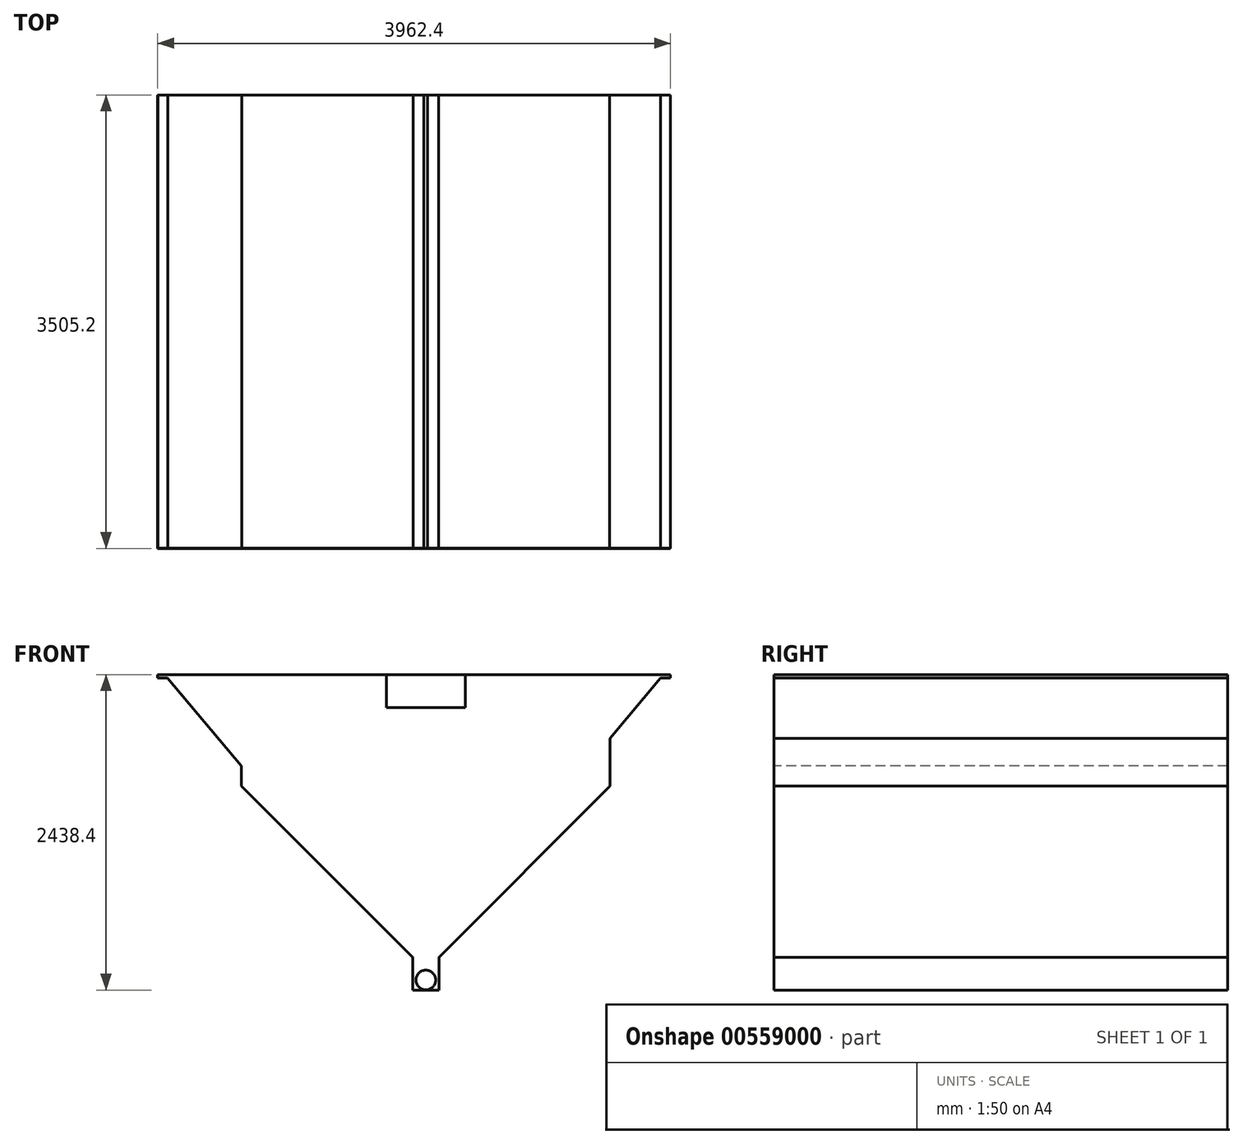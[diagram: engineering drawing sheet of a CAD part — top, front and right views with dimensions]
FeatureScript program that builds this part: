
annotation { "Feature Type Name" : "Feature", "Feature Type Description" : "" }
export const myFeature = defineFeature(function(context is Context, id is Id, definition is map)
    precondition{}
    {
        {
            var Q0;
            Q0=qCreatedBy(makeId("Front.planeOp"),FACE);
            var sketch = newSketch(context, id + "F0", { "sketchPlane" : qUnion([Q0])});
            skLineSegment(sketch, "E0", {"start": v(1891.4, 2159) * mm, "end": v(1891.4, 2184.4) * mm});
            skLineSegment(sketch, "E1", {"start": v(1891.4, 2159) * mm, "end": v(1815.2, 2159) * mm});
            skLineSegment(sketch, "E2", {"start": v(-1994.8, 2184.4) * mm, "end": v(-2071, 2184.4) * mm});
            skLineSegment(sketch, "E3", {"start": v(-2071, 2184.4) * mm, "end": v(-2071, 2159) * mm});
            skLineSegment(sketch, "E4", {"start": v(-2071, 2159) * mm, "end": v(-1994.8, 2159) * mm});
            skLineSegment(sketch, "E5", {"start": v(-1423.36, 1477.99) * mm, "end": v(-1994.8, 2159) * mm});
            skLineSegment(sketch, "E6", {"start": v(1891.4, 2184.4) * mm, "end": v(1815.2, 2184.4) * mm});
            skLineSegment(sketch, "E7", {"start": v(1815.2, 2184.4) * mm, "end": v(-1994.8, 2184.4) * mm});
            skLineSegment(sketch, "E8", {"start": v(1815.2, 2159) * mm, "end": v(1423.36, 1692.02) * mm});
            skLineSegment(sketch, "E9", {"start": v(-1423.36, 1477.99) * mm, "end": v(-1423.36, 1321.76) * mm});
            skLineSegment(sketch, "E10", {"start": v(1423.36, 1692.02) * mm, "end": v(1423.36, 1321.76) * mm});
            skLineSegment(sketch, "E11", {"start": v(0, 3707.85) * mm, "end": v(0, -913.4) * mm, "construction": true});
            skLineSegment(sketch, "E12", {"start": v(-1423.36, 1321.76) * mm, "end": v(-101.6, 0) * mm});
            skLineSegment(sketch, "E13", {"start": v(-101.6, 0) * mm, "end": v(-101.6, -254) * mm});
            skLineSegment(sketch, "E14", {"start": v(101.6, -254) * mm, "end": v(101.6, 0) * mm});
            skLineSegment(sketch, "E15", {"start": v(101.6, 0) * mm, "end": v(1423.36, 1321.76) * mm});
            skLineSegment(sketch, "E16", {"start": v(-1994.8, 2184.4) * mm, "end": v(-1994.8, 2159) * mm});
            skLineSegment(sketch, "E17", {"start": v(1815.2, 2184.4) * mm, "end": v(1815.2, 2159) * mm});
            skLineSegment(sketch, "E18", {"start": v(-101.6, -254) * mm, "end": v(101.6, -254) * mm});
            skSolve(sketch);
        }
        {
            var Q0;
            Q0 = qSketchRegion(id + "F0", true);
            extrude(context, id + "F1", {"entities" : qUnion([Q0]), "oppositeDirection" : true, "depth" : 3505.2 * mm, "offsetDistance" : 25.4 * mm});
        }
        {
            var Q0;
            Q0=makeQuery(id+"F1.opExtrude","SWEPT_FACE",FACE,{"disambiguationData":[OSD([sQuery(id+"F0.wireOp",EDGE,"E2"),sQuery(id+"F0.wireOp",EDGE,"E6"),sQuery(id+"F0.wireOp",EDGE,"E7")])]});
            shell(context, id + "F2", {"entities" : qUnion([Q0]), "thickness" : 2.54 * mm});
        }
        {
            var Q0;
            Q0=makeQuery(id+"F1.opExtrude","CAP_FACE",FACE,{"disambiguationData":[OSD([sQuery(id+"F0.wireOp",EDGE,"E0"),sQuery(id+"F0.wireOp",EDGE,"E1"),sQuery(id+"F0.wireOp",EDGE,"E2"),sQuery(id+"F0.wireOp",EDGE,"E3"),sQuery(id+"F0.wireOp",EDGE,"E4"),sQuery(id+"F0.wireOp",EDGE,"E5"),sQuery(id+"F0.wireOp",EDGE,"E6"),sQuery(id+"F0.wireOp",EDGE,"E7"),sQuery(id+"F0.wireOp",EDGE,"E8"),sQuery(id+"F0.wireOp",EDGE,"E9"),sQuery(id+"F0.wireOp",EDGE,"E10"),sQuery(id+"F0.wireOp",EDGE,"E12"),sQuery(id+"F0.wireOp",EDGE,"E13"),sQuery(id+"F0.wireOp",EDGE,"E14"),sQuery(id+"F0.wireOp",EDGE,"E15"),sQuery(id+"F0.wireOp",EDGE,"E18")])],"isStart":true});
            var sketch = newSketch(context, id + "F3", { "sketchPlane" : qUnion([Q0])});
            skCircle(sketch, "E19", {"center": v(0, -176.53) * mm, "radius": 76.2 * mm});
            skSolve(sketch);
        }
        {
            var Q0;
            Q0=makeQuery(id+"F3.imprint","IMPRINT",FACE,{"disambiguationData":[TD([[makeQuery(id+"F3.imprint","IMPRINT",EDGE,{"derivedFrom":sQuery(id+"F3.wireOp",EDGE,"E19")}),1.0]])]});
            extrude(context, id + "F4", {"entities" : qUnion([Q0]), "operationType" : NewBodyOperationType.REMOVE, "endBound" : BoundingType.THROUGH_ALL, "oppositeDirection" : true, "depth" : 25.4 * mm, "offsetDistance" : 25.4 * mm});
        }
        {
            var Q0;
            Q0=makeQuery(id+"F1.opExtrude","CAP_FACE",FACE,{"disambiguationData":[OSD([sQuery(id+"F0.wireOp",EDGE,"E0"),sQuery(id+"F0.wireOp",EDGE,"E1"),sQuery(id+"F0.wireOp",EDGE,"E2"),sQuery(id+"F0.wireOp",EDGE,"E3"),sQuery(id+"F0.wireOp",EDGE,"E4"),sQuery(id+"F0.wireOp",EDGE,"E5"),sQuery(id+"F0.wireOp",EDGE,"E6"),sQuery(id+"F0.wireOp",EDGE,"E7"),sQuery(id+"F0.wireOp",EDGE,"E8"),sQuery(id+"F0.wireOp",EDGE,"E9"),sQuery(id+"F0.wireOp",EDGE,"E10"),sQuery(id+"F0.wireOp",EDGE,"E12"),sQuery(id+"F0.wireOp",EDGE,"E13"),sQuery(id+"F0.wireOp",EDGE,"E14"),sQuery(id+"F0.wireOp",EDGE,"E15"),sQuery(id+"F0.wireOp",EDGE,"E18")])],"isStart":true});
            var sketch = newSketch(context, id + "F5", { "sketchPlane" : qUnion([Q0])});
            skLineSegment(sketch, "E20", {"start": v(-304.8, 2184.4) * mm, "end": v(304.8, 2184.4) * mm});
            skLineSegment(sketch, "E21", {"start": v(304.8, 2184.4) * mm, "end": v(304.8, 1930.4) * mm});
            skLineSegment(sketch, "E22", {"start": v(304.8, 1930.4) * mm, "end": v(-304.8, 1930.4) * mm});
            skLineSegment(sketch, "E23", {"start": v(-304.8, 1930.4) * mm, "end": v(-304.8, 2184.4) * mm});
            skLineSegment(sketch, "E24", {"start": v(0, 2527.33) * mm, "end": v(0, -492.35) * mm, "construction": true});
            skSolve(sketch);
        }
        {
            var Q0;
            Q0 = qSketchRegion(id + "F5", true);
            extrude(context, id + "F6", {"entities" : qUnion([Q0]), "operationType" : NewBodyOperationType.REMOVE, "oppositeDirection" : true, "depth" : 25.4 * mm, "offsetDistance" : 25.4 * mm});
        }
    });
